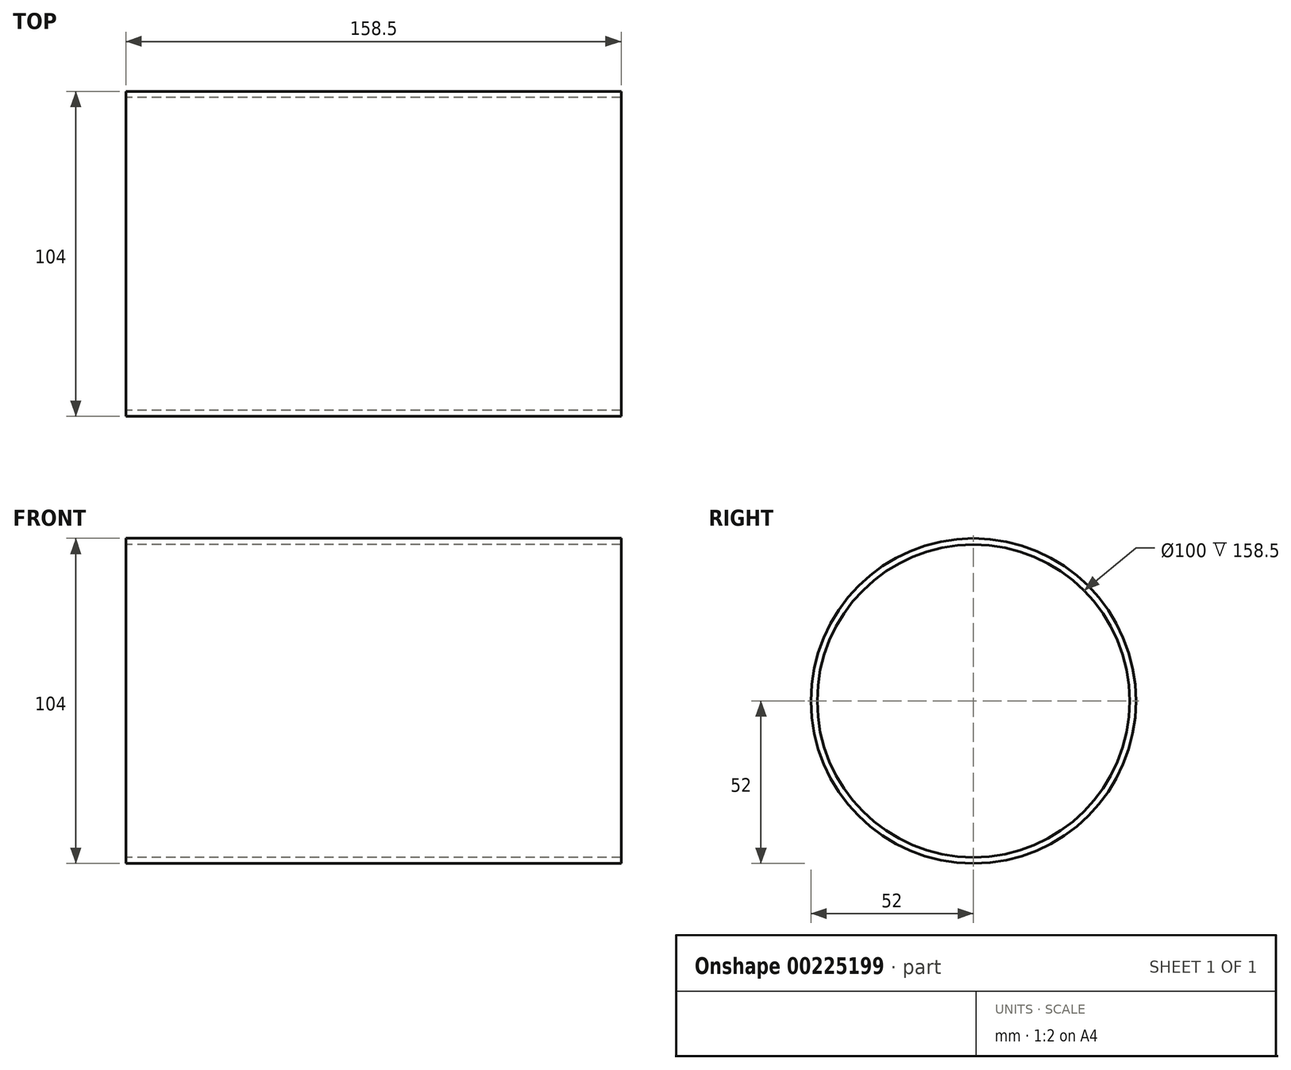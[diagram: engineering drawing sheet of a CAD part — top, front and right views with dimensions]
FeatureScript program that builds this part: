
annotation { "Feature Type Name" : "Feature", "Feature Type Description" : "" }
export const myFeature = defineFeature(function(context is Context, id is Id, definition is map)
    precondition{}
    {
        {
            var Q0;
            Q0=qCreatedBy(makeId("Right.planeOp"),FACE);
            var sketch = newSketch(context, id + "F0", { "sketchPlane" : qUnion([Q0])});
            skCircle(sketch, "E0", {"center": v(0, 0) * mm, "radius": 50 * mm});
            skCircle(sketch, "E1", {"center": v(0, 0) * mm, "radius": 52 * mm});
            skSolve(sketch);
        }
        {
            var Q0;
            Q0=makeQuery(id+"F0.imprint","IMPRINT",FACE,{"disambiguationData":[TD([[makeQuery(id+"F0.imprint","IMPRINT",EDGE,{"derivedFrom":sQuery(id+"F0.wireOp",EDGE,"E0")}),-1.0]])]});
            extrude(context, id + "F1", {"entities" : qUnion([Q0]), "depth" : 158.5 * mm});
        }
    });
